# Revit family: SH 4731-110W
name_source: partatom
category: Lighting Fixtures
revit_build: Autodesk Revit 2017 (Build: 20160225_1515(x64)
units: mm (PartAtom-declared; Revit-internal decimal feet)

## family parameters
Always vertical = Yes
Cut with Voids When Loaded = No
Host = Ceiling
Light Source = Yes
OmniClass Number = 23.80.70.11
OmniClass Title = Luminaries for Internal Lighting
Part Type = Normal
Room Calculation Point = No
Round Connector Dimension = Use Diameter
Shared = No

## types (2) — shared parameters
Body Material = Aluminum
Body color = Black Body
Color Filter = 16777215
Dimming Lamp Color Temperature Shift = <None>
IP = 66
Manufacturer = SHOA
Model = sh-4731-110w
Photometric Web File = FloodLight4730 60w 90D-R5m-code0-370(3).ies
Tilt Angle = 90.00°
URL = https://www.shoaco.com
Voltage/Frequency = 230V/50HZ
Website = www.shoaco.com
color temperature = 3000-6500K
consumption current = 1 A
instalation = Pendant Mounted
wattage. = 110 W

## per-type parameters (varying)
| type | Lamp | Type medule |
| SH-4731-110W(Black body-6500K-LED) | LED | SMD |
| SH-4731-110W(Black body-3000K-LED) | led | smd |

## geometry (parser evidence)
native form markers: Sweep x3
no freeform markers — native parametric forms only
